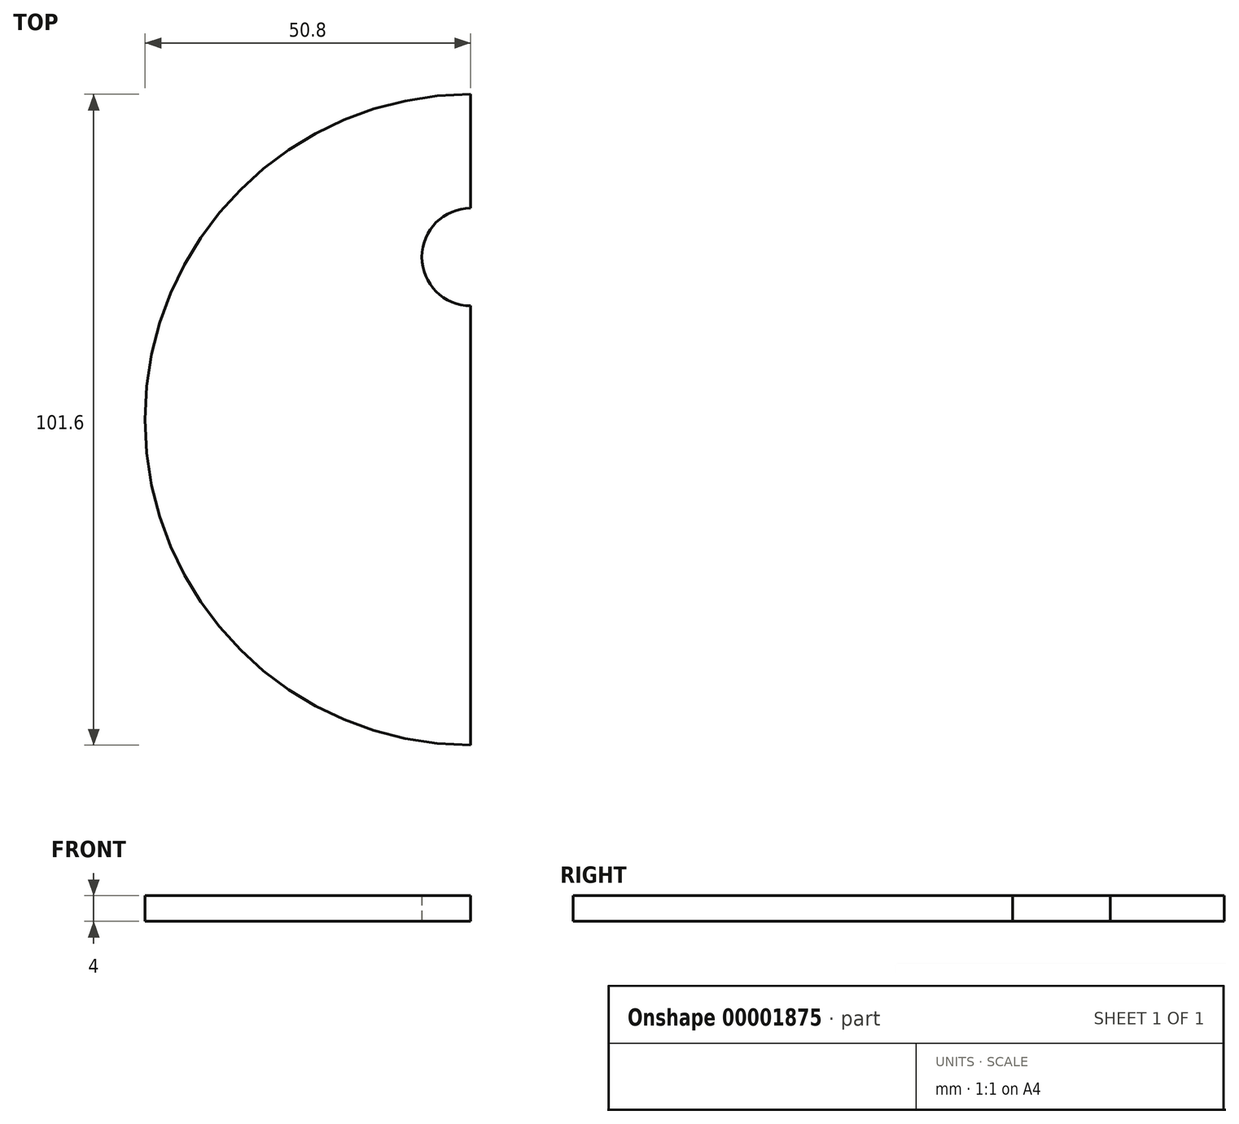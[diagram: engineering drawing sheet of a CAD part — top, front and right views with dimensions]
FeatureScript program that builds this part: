
annotation { "Feature Type Name" : "Feature", "Feature Type Description" : "" }
export const myFeature = defineFeature(function(context is Context, id is Id, definition is map)
    precondition{}
    {
        {
            var Q0;
            Q0=qCreatedBy(makeId("Top.planeOp"),FACE);
            var sketch = newSketch(context, id + "F0", { "sketchPlane" : qUnion([Q0])});
            skLineSegment(sketch, "E0", {"start": v(-107.95, 139.7) * mm, "end": v(107.95, 139.7) * mm});
            skLineSegment(sketch, "E1", {"start": v(-107.95, -139.7) * mm, "end": v(107.95, -139.7) * mm});
            skLineSegment(sketch, "E2", {"start": v(-100.08, 129.03) * mm, "end": v(100.08, 129.03) * mm});
            skLineSegment(sketch, "E3", {"start": v(-93.73, 122.68) * mm, "end": v(93.73, 122.68) * mm});
            skLineSegment(sketch, "E4", {"start": v(0, -50.8) * mm, "end": v(0, 17.78) * mm});
            skLineSegment(sketch, "E5", {"start": v(0, 33.02) * mm, "end": v(0, 50.8) * mm});
            skLineSegment(sketch, "E6", {"start": v(0, -50.8) * mm, "end": v(0, 50.8) * mm, "construction": true});
            skEllipticalArc(sketch, "E7", {});
            skArc(sketch, "E8", {"start": v(0, -50.8) * mm, "mid": v(-50.8, 0) * mm, "end": v(0, 50.8) * mm});
            const initialGuessF0  = {"E7": [0, 0.0254, 0, 1, 0.00762, 0.00762, 0, 3.141592653589793]};
            skSetInitialGuess(sketch, initialGuessF0);
            skSolve(sketch);
        }
        {
            var Q0;
            Q0 = qSketchRegion(id + "F0", true);
            extrude(context, id + "F1", {"entities" : qUnion([Q0]), "depth" : 4 * mm});
        }
    });
